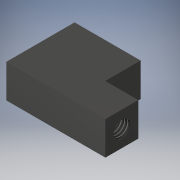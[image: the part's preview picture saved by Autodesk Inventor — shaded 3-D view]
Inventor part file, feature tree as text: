
AUTODESK INVENTOR PART (.ipt)
format: ipt  version: 2018.3 (Build 223285000, 285)  size: 157,184 bytes
history: native  units: mm
features: thread x4, imported_body x1
ambient origin geometry x8: Origin, YZ Plane, XZ Plane, XY Plane, X Axis, Y Axis, Z Axis, Center Point
bodies: Solid1 (feature_tree)
feature tree (5):
  imported_body  "Base1"
  thread  "Thread1"  [1 undecoded]
  thread  "Thread2"  [1 undecoded]
  thread  "Thread3"  [1 undecoded]
  thread  "Thread4"  [1 undecoded]
note: 4 required parameter values undecoded (feature->parameter linkage not recoverable at this tier; creation-order binding heuristic only, values carry confidence <= 0.55)
